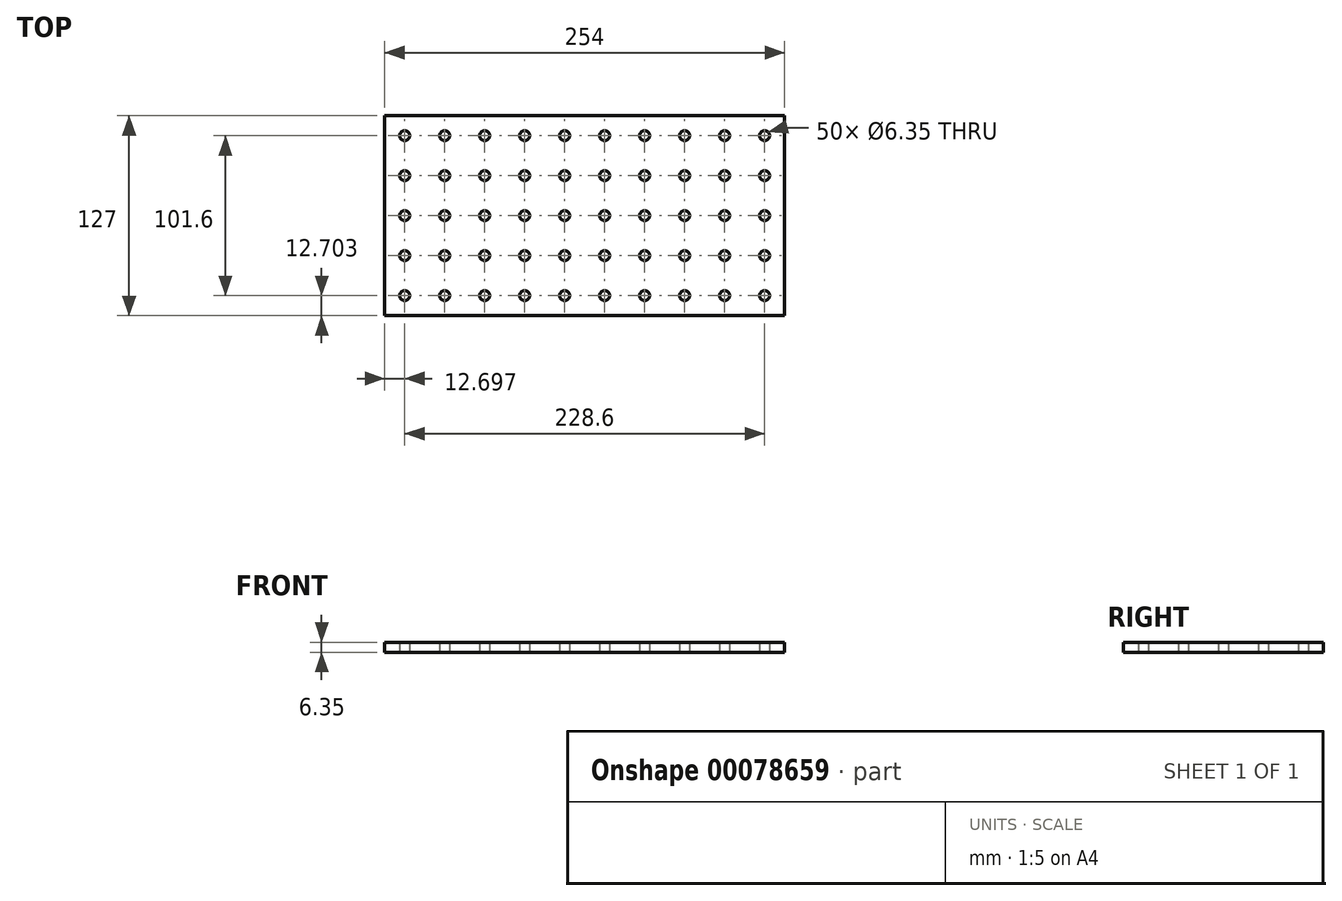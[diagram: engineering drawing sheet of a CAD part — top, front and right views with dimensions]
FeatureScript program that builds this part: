
annotation { "Feature Type Name" : "Feature", "Feature Type Description" : "" }
export const myFeature = defineFeature(function(context is Context, id is Id, definition is map)
    precondition{}
    {
        {
            var Q0;
            Q0=qCreatedBy(makeId("Top.planeOp"),FACE);
            var sketch = newSketch(context, id + "F0", { "sketchPlane" : qUnion([Q0])});
            skLineSegment(sketch, "E0.bottom", {"start": v(-119.27, 89.75) * mm, "end": v(134.73, 89.75) * mm});
            skLineSegment(sketch, "E0.top", {"start": v(-119.27, -37.25) * mm, "end": v(134.73, -37.25) * mm});
            skLineSegment(sketch, "E0.left", {"start": v(-119.27, 89.75) * mm, "end": v(-119.27, -37.25) * mm});
            skLineSegment(sketch, "E0.right", {"start": v(134.73, 89.75) * mm, "end": v(134.73, -37.25) * mm});
            skCircle(sketch, "E1", {"center": v(-106.57, 77.05) * mm, "radius": 3.18 * mm});
            skCircle(sketch, "E2.0.1.0", {"center": v(-106.57, 51.65) * mm, "radius": 3.18 * mm});
            skCircle(sketch, "E2.0.2.0", {"center": v(-106.57, 26.25) * mm, "radius": 3.18 * mm});
            skCircle(sketch, "E2.1.0.0", {"center": v(-81.17, 77.05) * mm, "radius": 3.18 * mm});
            skCircle(sketch, "E2.1.1.0", {"center": v(-81.17, 51.65) * mm, "radius": 3.18 * mm});
            skCircle(sketch, "E2.1.2.0", {"center": v(-81.17, 26.25) * mm, "radius": 3.18 * mm});
            skCircle(sketch, "E2.2.0.0", {"center": v(-55.77, 77.05) * mm, "radius": 3.18 * mm});
            skCircle(sketch, "E2.2.1.0", {"center": v(-55.77, 51.65) * mm, "radius": 3.18 * mm});
            skCircle(sketch, "E2.2.2.0", {"center": v(-55.77, 26.25) * mm, "radius": 3.18 * mm});
            skCircle(sketch, "E2.3.0.0", {"center": v(-30.37, 77.05) * mm, "radius": 3.18 * mm});
            skCircle(sketch, "E2.3.1.0", {"center": v(-30.37, 51.65) * mm, "radius": 3.18 * mm});
            skCircle(sketch, "E2.3.2.0", {"center": v(-30.37, 26.25) * mm, "radius": 3.18 * mm});
            skCircle(sketch, "E2.4.0.0", {"center": v(-4.97, 77.05) * mm, "radius": 3.18 * mm});
            skCircle(sketch, "E2.4.1.0", {"center": v(-4.97, 51.65) * mm, "radius": 3.18 * mm});
            skCircle(sketch, "E2.4.2.0", {"center": v(-4.97, 26.25) * mm, "radius": 3.18 * mm});
            skCircle(sketch, "E2.5.0.0", {"center": v(20.43, 77.05) * mm, "radius": 3.18 * mm});
            skCircle(sketch, "E2.5.1.0", {"center": v(20.43, 51.65) * mm, "radius": 3.18 * mm});
            skCircle(sketch, "E2.5.2.0", {"center": v(20.43, 26.25) * mm, "radius": 3.18 * mm});
            skCircle(sketch, "E2.6.0.0", {"center": v(45.83, 77.05) * mm, "radius": 3.18 * mm});
            skCircle(sketch, "E2.6.1.0", {"center": v(45.83, 51.65) * mm, "radius": 3.18 * mm});
            skCircle(sketch, "E2.6.2.0", {"center": v(45.83, 26.25) * mm, "radius": 3.18 * mm});
            skCircle(sketch, "E2.7.0.0", {"center": v(71.23, 77.05) * mm, "radius": 3.18 * mm});
            skCircle(sketch, "E2.7.1.0", {"center": v(71.23, 51.65) * mm, "radius": 3.18 * mm});
            skCircle(sketch, "E2.7.2.0", {"center": v(71.23, 26.25) * mm, "radius": 3.18 * mm});
            skCircle(sketch, "E2.8.0.0", {"center": v(96.63, 77.05) * mm, "radius": 3.18 * mm});
            skCircle(sketch, "E2.8.1.0", {"center": v(96.63, 51.65) * mm, "radius": 3.18 * mm});
            skCircle(sketch, "E2.8.2.0", {"center": v(96.63, 26.25) * mm, "radius": 3.18 * mm});
            skLineSegment(sketch, "E2.direction1", {"start": v(-106.57, 77.05) * mm, "end": v(-81.17, 77.05) * mm, "construction": true});
            skLineSegment(sketch, "E2.direction2", {"start": v(-106.57, 77.05) * mm, "end": v(-106.57, 51.65) * mm, "construction": true});
            skCircle(sketch, "E3.0.0.3", {"center": v(-106.57, 0.85) * mm, "radius": 3.18 * mm});
            skCircle(sketch, "E3.0.0.4", {"center": v(-106.57, -24.55) * mm, "radius": 3.18 * mm});
            skCircle(sketch, "E3.0.1.3", {"center": v(-81.17, 0.85) * mm, "radius": 3.18 * mm});
            skCircle(sketch, "E3.0.1.4", {"center": v(-81.17, -24.55) * mm, "radius": 3.18 * mm});
            skCircle(sketch, "E3.0.2.3", {"center": v(-55.77, 0.85) * mm, "radius": 3.18 * mm});
            skCircle(sketch, "E3.0.2.4", {"center": v(-55.77, -24.55) * mm, "radius": 3.18 * mm});
            skCircle(sketch, "E3.0.3.3", {"center": v(-30.37, 0.85) * mm, "radius": 3.18 * mm});
            skCircle(sketch, "E3.0.3.4", {"center": v(-30.37, -24.55) * mm, "radius": 3.18 * mm});
            skCircle(sketch, "E3.0.4.3", {"center": v(-4.97, 0.85) * mm, "radius": 3.18 * mm});
            skCircle(sketch, "E3.0.4.4", {"center": v(-4.97, -24.55) * mm, "radius": 3.18 * mm});
            skCircle(sketch, "E3.0.5.3", {"center": v(20.43, 0.85) * mm, "radius": 3.18 * mm});
            skCircle(sketch, "E3.0.5.4", {"center": v(20.43, -24.55) * mm, "radius": 3.18 * mm});
            skCircle(sketch, "E3.0.6.3", {"center": v(45.83, 0.85) * mm, "radius": 3.18 * mm});
            skCircle(sketch, "E3.0.6.4", {"center": v(45.83, -24.55) * mm, "radius": 3.18 * mm});
            skCircle(sketch, "E3.0.7.3", {"center": v(71.23, 0.85) * mm, "radius": 3.18 * mm});
            skCircle(sketch, "E3.0.7.4", {"center": v(71.23, -24.55) * mm, "radius": 3.18 * mm});
            skCircle(sketch, "E3.0.8.3", {"center": v(96.63, 0.85) * mm, "radius": 3.18 * mm});
            skCircle(sketch, "E3.0.8.4", {"center": v(96.63, -24.55) * mm, "radius": 3.18 * mm});
            skCircle(sketch, "E4.0.9.0", {"center": v(122.03, 77.05) * mm, "radius": 3.18 * mm});
            skCircle(sketch, "E4.0.9.1", {"center": v(122.03, 51.65) * mm, "radius": 3.18 * mm});
            skCircle(sketch, "E4.0.9.2", {"center": v(122.03, 26.25) * mm, "radius": 3.18 * mm});
            skCircle(sketch, "E4.0.9.3", {"center": v(122.03, 0.85) * mm, "radius": 3.18 * mm});
            skCircle(sketch, "E4.0.9.4", {"center": v(122.03, -24.55) * mm, "radius": 3.18 * mm});
            skSolve(sketch);
        }
        {
            var Q0;
            Q0 = qSketchRegion(id + "F0", true);
            extrude(context, id + "F1", {"entities" : qUnion([Q0]), "depth" : 6.35 * mm});
        }
    });
